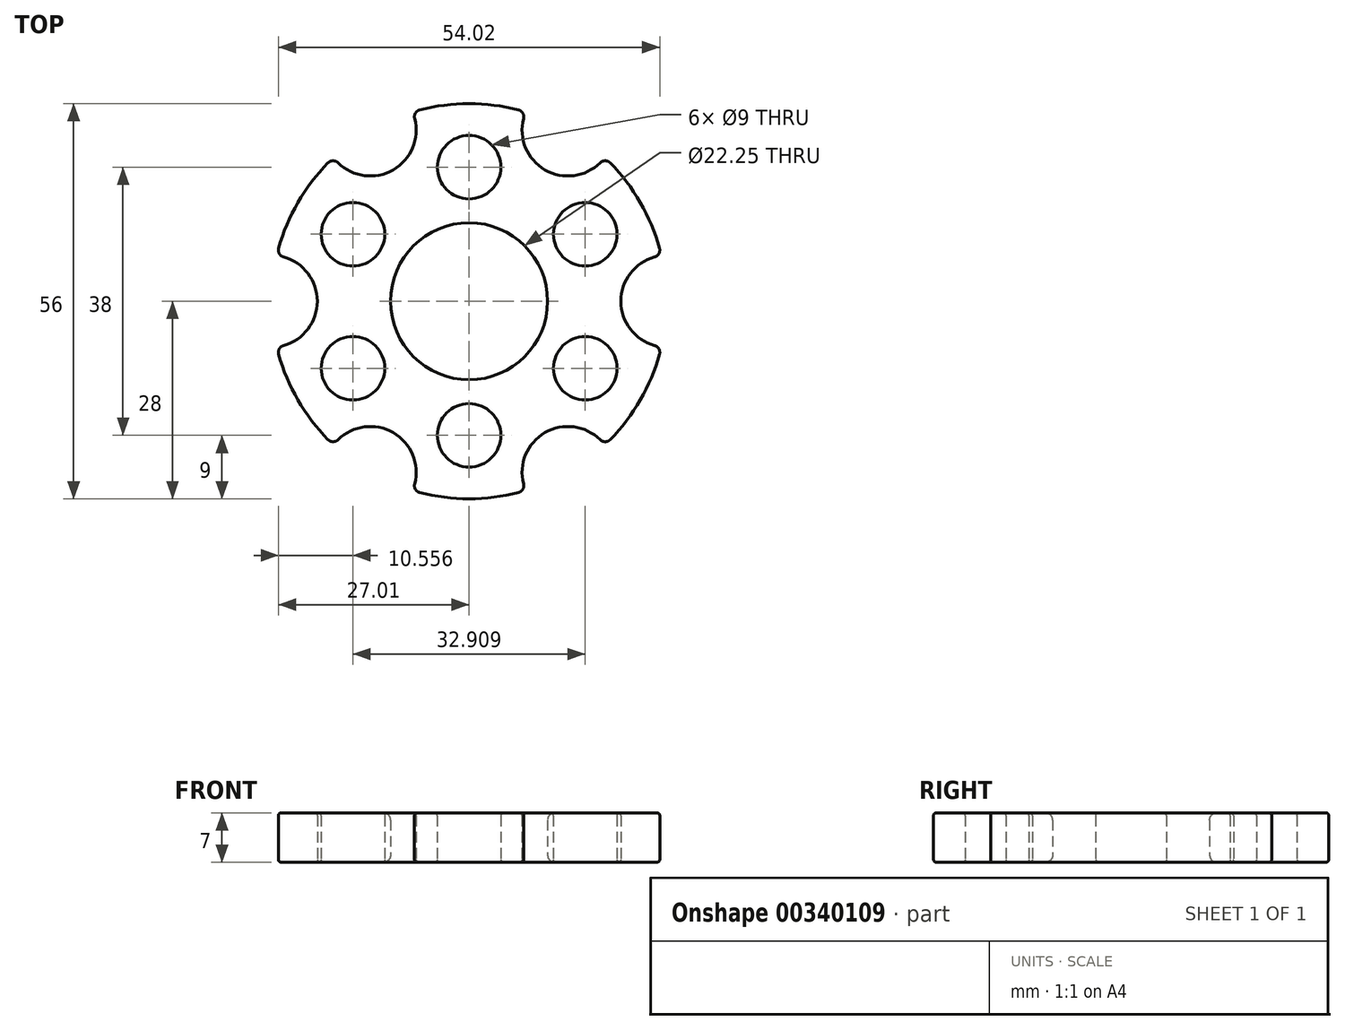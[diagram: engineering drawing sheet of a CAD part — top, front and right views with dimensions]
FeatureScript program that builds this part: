
annotation { "Feature Type Name" : "Feature", "Feature Type Description" : "" }
export const myFeature = defineFeature(function(context is Context, id is Id, definition is map)
    precondition{}
    {
        {
            var Q0;
            Q0=qCreatedBy(makeId("Top.planeOp"),FACE);
            var sketch = newSketch(context, id + "F0", { "sketchPlane" : qUnion([Q0])});
            skArc(sketch, "E0", {"start": v(-19.98, 19.61) * mm, "mid": v(-24.25, 14) * mm, "end": v(-26.98, 7.5) * mm});
            skCircle(sketch, "E1", {"center": v(0, 0) * mm, "radius": 11.12 * mm});
            skCircle(sketch, "E2", {"center": v(0, 19) * mm, "radius": 4.5 * mm});
            skCircle(sketch, "E3.1.0", {"center": v(-16.45, 9.5) * mm, "radius": 4.5 * mm});
            skCircle(sketch, "E3.2.0", {"center": v(-16.45, -9.5) * mm, "radius": 4.5 * mm});
            skCircle(sketch, "E3.3.0", {"center": v(0, -19) * mm, "radius": 4.5 * mm});
            skCircle(sketch, "E3.4.0", {"center": v(16.45, -9.5) * mm, "radius": 4.5 * mm});
            skCircle(sketch, "E3.5.0", {"center": v(16.45, 9.5) * mm, "radius": 4.5 * mm});
            skArc(sketch, "E4", {"start": v(-26.28, -6.27) * mm, "mid": v(-21.5, 0) * mm, "end": v(-26.28, 6.27) * mm});
            skArc(sketch, "E5.1.0", {"start": v(-7.71, -25.9) * mm, "mid": v(-10.75, -18.62) * mm, "end": v(-18.57, -19.62) * mm});
            skArc(sketch, "E5.2.0", {"start": v(18.57, -19.62) * mm, "mid": v(10.75, -18.62) * mm, "end": v(7.71, -25.9) * mm});
            skArc(sketch, "E5.3.0", {"start": v(26.28, 6.27) * mm, "mid": v(21.5, 0) * mm, "end": v(26.28, -6.27) * mm});
            skArc(sketch, "E5.4.0", {"start": v(7.71, 25.9) * mm, "mid": v(10.75, 18.62) * mm, "end": v(18.57, 19.62) * mm});
            skArc(sketch, "E5.5.0", {"start": v(-18.57, 19.62) * mm, "mid": v(-10.75, 18.62) * mm, "end": v(-7.71, 25.9) * mm});
            skArc(sketch, "E6.trimOffspring", {"start": v(7, 27.11) * mm, "mid": v(0, 28) * mm, "end": v(-7, 27.11) * mm});
            skArc(sketch, "E7.trimOffspring", {"start": v(26.98, 7.5) * mm, "mid": v(24.25, 14) * mm, "end": v(19.98, 19.61) * mm});
            skArc(sketch, "E8.trimOffspring", {"start": v(19.98, -19.61) * mm, "mid": v(24.25, -14) * mm, "end": v(26.98, -7.5) * mm});
            skArc(sketch, "E9.trimOffspring", {"start": v(-7, -27.11) * mm, "mid": v(0, -28) * mm, "end": v(7, -27.11) * mm});
            skArc(sketch, "E10.trimOffspring", {"start": v(-26.98, -7.5) * mm, "mid": v(-24.25, -14) * mm, "end": v(-19.98, -19.61) * mm});
            skPoint(sketch, "E11.visualSharp", {"position": v(-8.03, 26.82) * mm});
            skArc(sketch, "E11.filletArc", {"start": v(-7, 27.11) * mm, "mid": v(-7.6, 26.65) * mm, "end": v(-7.71, 25.9) * mm});
            skPoint(sketch, "E12.visualSharp", {"position": v(8.03, 26.82) * mm});
            skArc(sketch, "E12.filletArc", {"start": v(7.71, 25.9) * mm, "mid": v(7.6, 26.65) * mm, "end": v(7, 27.11) * mm});
            skPoint(sketch, "E13.visualSharp", {"position": v(19.21, 20.37) * mm});
            skArc(sketch, "E13.filletArc", {"start": v(19.98, 19.61) * mm, "mid": v(19.28, 19.91) * mm, "end": v(18.57, 19.62) * mm});
            skPoint(sketch, "E14.visualSharp", {"position": v(27.25, 6.46) * mm});
            skArc(sketch, "E14.filletArc", {"start": v(26.28, 6.27) * mm, "mid": v(26.88, 6.74) * mm, "end": v(26.98, 7.5) * mm});
            skPoint(sketch, "E15.visualSharp", {"position": v(27.25, -6.46) * mm});
            skArc(sketch, "E15.filletArc", {"start": v(26.98, -7.5) * mm, "mid": v(26.88, -6.74) * mm, "end": v(26.28, -6.27) * mm});
            skPoint(sketch, "E16.visualSharp", {"position": v(19.21, -20.37) * mm});
            skArc(sketch, "E16.filletArc", {"start": v(18.57, -19.62) * mm, "mid": v(19.28, -19.91) * mm, "end": v(19.98, -19.61) * mm});
            skPoint(sketch, "E17.visualSharp", {"position": v(8.03, -26.82) * mm});
            skArc(sketch, "E17.filletArc", {"start": v(7, -27.11) * mm, "mid": v(7.6, -26.65) * mm, "end": v(7.71, -25.9) * mm});
            skPoint(sketch, "E18.visualSharp", {"position": v(-8.03, -26.82) * mm});
            skArc(sketch, "E18.filletArc", {"start": v(-7.71, -25.9) * mm, "mid": v(-7.6, -26.65) * mm, "end": v(-7, -27.11) * mm});
            skPoint(sketch, "E19.visualSharp", {"position": v(-19.21, -20.37) * mm});
            skArc(sketch, "E19.filletArc", {"start": v(-19.98, -19.61) * mm, "mid": v(-19.28, -19.91) * mm, "end": v(-18.57, -19.62) * mm});
            skPoint(sketch, "E20.visualSharp", {"position": v(-27.25, -6.46) * mm});
            skArc(sketch, "E20.filletArc", {"start": v(-26.28, -6.27) * mm, "mid": v(-26.88, -6.74) * mm, "end": v(-26.98, -7.5) * mm});
            skPoint(sketch, "E21.visualSharp", {"position": v(-27.25, 6.46) * mm});
            skArc(sketch, "E21.filletArc", {"start": v(-26.98, 7.5) * mm, "mid": v(-26.88, 6.74) * mm, "end": v(-26.28, 6.27) * mm});
            skPoint(sketch, "E22.visualSharp", {"position": v(-19.21, 20.37) * mm});
            skArc(sketch, "E22.filletArc", {"start": v(-18.57, 19.62) * mm, "mid": v(-19.28, 19.91) * mm, "end": v(-19.98, 19.61) * mm});
            skSolve(sketch);
        }
        {
            var Q0;
            Q0=qSketchRegion(id+"F0",true);
            extrude(context, id + "F1", {"entities" : qUnion([Q0]), "depth" : 7 * mm});
        }
        {
            var Q0;
            Q0=makeQuery(id+"F1.opExtrude","SWEPT_FACE",FACE,{"disambiguationData":[OSD([sQuery(id+"F0.wireOp",EDGE,"E1")])]});
            fillet(context, id + "F2", {"entities" : qUnion([Q0]), "radius" : 1 * mm, "tangentPropagation" : true, "allowEdgeOverflow" : false});
        }
        {
            var Q0;
            Q0=makeQuery(id+"F1.opExtrude","CAP_FACE",FACE,{"disambiguationData":[OSD([sQuery(id+"F0.wireOp",EDGE,"E0"),sQuery(id+"F0.wireOp",EDGE,"E1"),sQuery(id+"F0.wireOp",EDGE,"E2"),sQuery(id+"F0.wireOp",EDGE,"E3.1.0"),sQuery(id+"F0.wireOp",EDGE,"E3.2.0"),sQuery(id+"F0.wireOp",EDGE,"E3.3.0"),sQuery(id+"F0.wireOp",EDGE,"E3.4.0"),sQuery(id+"F0.wireOp",EDGE,"E3.5.0"),sQuery(id+"F0.wireOp",EDGE,"E4"),sQuery(id+"F0.wireOp",EDGE,"E5.1.0"),sQuery(id+"F0.wireOp",EDGE,"E5.2.0"),sQuery(id+"F0.wireOp",EDGE,"E5.3.0"),sQuery(id+"F0.wireOp",EDGE,"E5.4.0"),sQuery(id+"F0.wireOp",EDGE,"E5.5.0"),sQuery(id+"F0.wireOp",EDGE,"E6.trimOffspring"),sQuery(id+"F0.wireOp",EDGE,"E7.trimOffspring"),sQuery(id+"F0.wireOp",EDGE,"E8.trimOffspring"),sQuery(id+"F0.wireOp",EDGE,"E9.trimOffspring"),sQuery(id+"F0.wireOp",EDGE,"E10.trimOffspring"),sQuery(id+"F0.wireOp",EDGE,"E11.filletArc"),sQuery(id+"F0.wireOp",EDGE,"E12.filletArc"),sQuery(id+"F0.wireOp",EDGE,"E13.filletArc"),sQuery(id+"F0.wireOp",EDGE,"E14.filletArc"),sQuery(id+"F0.wireOp",EDGE,"E15.filletArc"),sQuery(id+"F0.wireOp",EDGE,"E16.filletArc"),sQuery(id+"F0.wireOp",EDGE,"E17.filletArc"),sQuery(id+"F0.wireOp",EDGE,"E18.filletArc"),sQuery(id+"F0.wireOp",EDGE,"E19.filletArc"),sQuery(id+"F0.wireOp",EDGE,"E20.filletArc"),sQuery(id+"F0.wireOp",EDGE,"E21.filletArc"),sQuery(id+"F0.wireOp",EDGE,"E22.filletArc")])],"isStart":false});
            var Q1;
            Q1=makeQuery(id+"F1.opExtrude","CAP_FACE",FACE,{"disambiguationData":[OSD([sQuery(id+"F0.wireOp",EDGE,"E0"),sQuery(id+"F0.wireOp",EDGE,"E1"),sQuery(id+"F0.wireOp",EDGE,"E2"),sQuery(id+"F0.wireOp",EDGE,"E3.1.0"),sQuery(id+"F0.wireOp",EDGE,"E3.2.0"),sQuery(id+"F0.wireOp",EDGE,"E3.3.0"),sQuery(id+"F0.wireOp",EDGE,"E3.4.0"),sQuery(id+"F0.wireOp",EDGE,"E3.5.0"),sQuery(id+"F0.wireOp",EDGE,"E4"),sQuery(id+"F0.wireOp",EDGE,"E5.1.0"),sQuery(id+"F0.wireOp",EDGE,"E5.2.0"),sQuery(id+"F0.wireOp",EDGE,"E5.3.0"),sQuery(id+"F0.wireOp",EDGE,"E5.4.0"),sQuery(id+"F0.wireOp",EDGE,"E5.5.0"),sQuery(id+"F0.wireOp",EDGE,"E6.trimOffspring"),sQuery(id+"F0.wireOp",EDGE,"E7.trimOffspring"),sQuery(id+"F0.wireOp",EDGE,"E8.trimOffspring"),sQuery(id+"F0.wireOp",EDGE,"E9.trimOffspring"),sQuery(id+"F0.wireOp",EDGE,"E10.trimOffspring"),sQuery(id+"F0.wireOp",EDGE,"E11.filletArc"),sQuery(id+"F0.wireOp",EDGE,"E12.filletArc"),sQuery(id+"F0.wireOp",EDGE,"E13.filletArc"),sQuery(id+"F0.wireOp",EDGE,"E14.filletArc"),sQuery(id+"F0.wireOp",EDGE,"E15.filletArc"),sQuery(id+"F0.wireOp",EDGE,"E16.filletArc"),sQuery(id+"F0.wireOp",EDGE,"E17.filletArc"),sQuery(id+"F0.wireOp",EDGE,"E18.filletArc"),sQuery(id+"F0.wireOp",EDGE,"E19.filletArc"),sQuery(id+"F0.wireOp",EDGE,"E20.filletArc"),sQuery(id+"F0.wireOp",EDGE,"E21.filletArc"),sQuery(id+"F0.wireOp",EDGE,"E22.filletArc")])],"isStart":true});
            fillet(context, id + "F3", {"entities" : qUnion([Q0, Q1]), "radius" : .4 * mm, "tangentPropagation" : true, "allowEdgeOverflow" : false});
        }
    });
